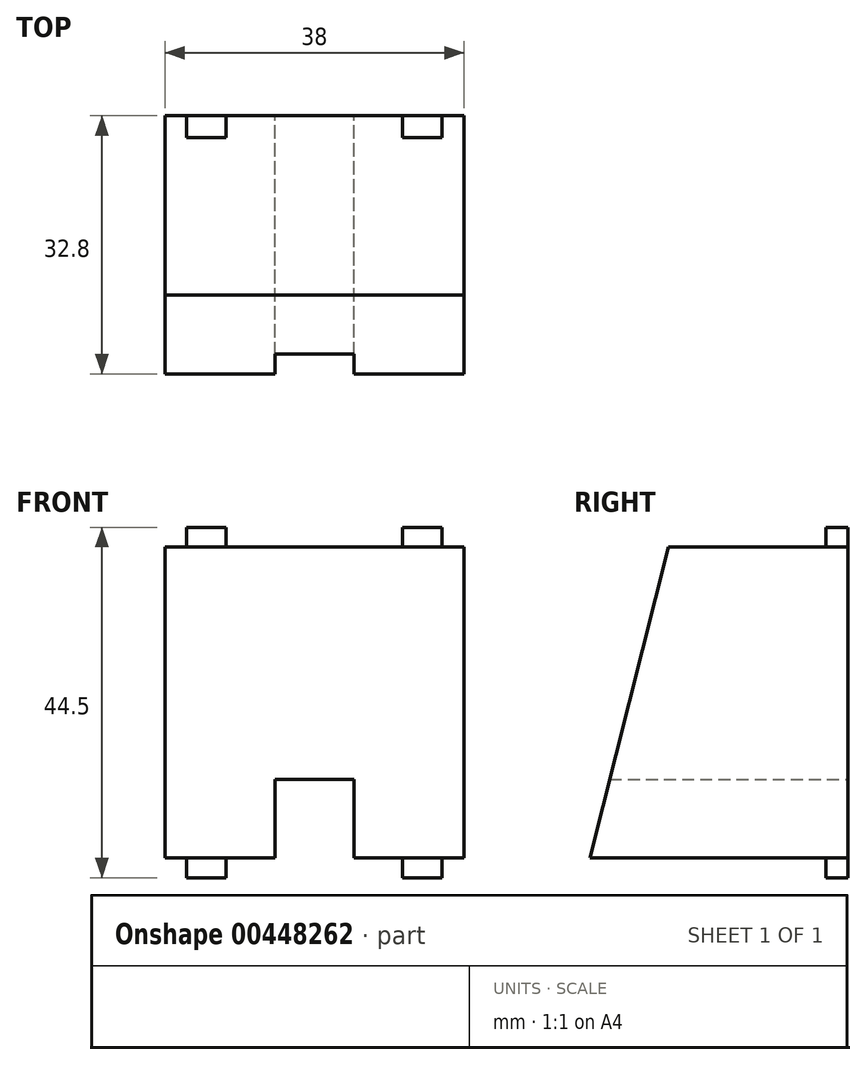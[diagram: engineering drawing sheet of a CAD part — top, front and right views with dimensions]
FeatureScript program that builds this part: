
annotation { "Feature Type Name" : "Feature", "Feature Type Description" : "" }
export const myFeature = defineFeature(function(context is Context, id is Id, definition is map)
    precondition{}
    {
        {
            var Q0;
            Q0=qCreatedBy(makeId("Front.planeOp"),FACE);
            var sketch = newSketch(context, id + "F0", { "sketchPlane" : qUnion([Q0])});
            skLineSegment(sketch, "E0", {"start": v(0, 0) * mm, "end": v(-11.22, 0) * mm});
            skLineSegment(sketch, "E1", {"start": v(-11.22, 0) * mm, "end": v(-11.22, 2.5) * mm});
            skLineSegment(sketch, "E2", {"start": v(-11.22, 2.5) * mm, "end": v(-16.22, 2.5) * mm});
            skLineSegment(sketch, "E3", {"start": v(-16.22, 2.5) * mm, "end": v(-16.22, 0) * mm});
            skLineSegment(sketch, "E4", {"start": v(-16.22, 0) * mm, "end": v(-19, 0) * mm});
            skLineSegment(sketch, "E5", {"start": v(-19, 0) * mm, "end": v(-19, -39.5) * mm});
            skLineSegment(sketch, "E6", {"start": v(-19, -39.5) * mm, "end": v(-16.22, -39.5) * mm});
            skLineSegment(sketch, "E7", {"start": v(-16.22, -39.5) * mm, "end": v(-16.22, -42) * mm});
            skLineSegment(sketch, "E8", {"start": v(-16.22, -42) * mm, "end": v(-11.22, -42) * mm});
            skLineSegment(sketch, "E9", {"start": v(-11.22, -42) * mm, "end": v(-11.22, -39.5) * mm});
            skLineSegment(sketch, "E10", {"start": v(-11.22, -39.5) * mm, "end": v(0, -39.5) * mm});
            skLineSegment(sketch, "E11.MirrorCS", {"start": v(11.22, 0) * mm, "end": v(11.22, 2.5) * mm});
            skLineSegment(sketch, "E12.MirrorCS", {"start": v(11.22, -42) * mm, "end": v(11.22, -39.5) * mm});
            skLineSegment(sketch, "E13.MirrorCS", {"start": v(16.22, 0) * mm, "end": v(19, 0) * mm});
            skLineSegment(sketch, "E14.MirrorCS", {"start": v(16.22, -42) * mm, "end": v(11.22, -42) * mm});
            skLineSegment(sketch, "E15.MirrorCS", {"start": v(19, 0) * mm, "end": v(19, -39.5) * mm});
            skLineSegment(sketch, "E16.MirrorCS", {"start": v(11.22, 2.5) * mm, "end": v(16.22, 2.5) * mm});
            skLineSegment(sketch, "E17.MirrorCS", {"start": v(19, -39.5) * mm, "end": v(16.22, -39.5) * mm});
            skLineSegment(sketch, "E18.MirrorCS", {"start": v(16.22, 2.5) * mm, "end": v(16.22, 0) * mm});
            skLineSegment(sketch, "E19.MirrorCS", {"start": v(16.22, -39.5) * mm, "end": v(16.22, -42) * mm});
            skLineSegment(sketch, "E20.MirrorCS", {"start": v(11.22, -39.5) * mm, "end": v(0, -39.5) * mm});
            skLineSegment(sketch, "E21.MirrorCS", {"start": v(0, 0) * mm, "end": v(11.22, 0) * mm});
            skLineSegment(sketch, "E22", {"start": v(-16.22, 0) * mm, "end": v(-11.22, 0) * mm});
            skLineSegment(sketch, "E23", {"start": v(11.22, 0) * mm, "end": v(16.22, 0) * mm});
            skLineSegment(sketch, "E24", {"start": v(-16.22, -39.5) * mm, "end": v(-11.22, -39.5) * mm});
            skLineSegment(sketch, "E25", {"start": v(11.22, -39.5) * mm, "end": v(16.22, -39.5) * mm});
            skSolve(sketch);
        }
        {
            var Q0;
            Q0=makeQuery(id+"F0.imprint","IMPRINT",FACE,{"disambiguationData":[TD([[makeQuery(id+"F0.imprint","IMPRINT",EDGE,{"derivedFrom":sQuery(id+"F0.wireOp",EDGE,"E1")}),1.0]])]});
            var Q1;
            Q1=makeQuery(id+"F0.imprint","IMPRINT",FACE,{"disambiguationData":[TD([[makeQuery(id+"F0.imprint","IMPRINT",EDGE,{"derivedFrom":sQuery(id+"F0.wireOp",EDGE,"E11.MirrorCS")}),-1.0]])]});
            var Q2;
            Q2=makeQuery(id+"F0.imprint","IMPRINT",FACE,{"disambiguationData":[TD([[makeQuery(id+"F0.imprint","IMPRINT",EDGE,{"derivedFrom":sQuery(id+"F0.wireOp",EDGE,"E7")}),1.0]])]});
            var Q3;
            Q3=makeQuery(id+"F0.imprint","IMPRINT",FACE,{"disambiguationData":[TD([[makeQuery(id+"F0.imprint","IMPRINT",EDGE,{"derivedFrom":sQuery(id+"F0.wireOp",EDGE,"E12.MirrorCS")}),-1.0]])]});
            var Q4;
            Q4=makeQuery(id+"F0.imprint","IMPRINT",FACE,{"disambiguationData":[TD([[makeQuery(id+"F0.imprint","IMPRINT",EDGE,{"derivedFrom":sQuery(id+"F0.wireOp",EDGE,"E0")}),1.0]])]});
            extrude(context, id + "F1", {"entities" : qUnion([Q0, Q1, Q2, Q3, Q4]), "depth" : 2.8 * mm});
        }
        {
            var Q0;
            Q0=makeQuery(id+"F1.opExtrude","SWEPT_FACE",FACE,{"disambiguationData":[OSD([sQuery(id+"F0.wireOp",EDGE,"E5")])]});
            var sketch = newSketch(context, id + "F2", { "sketchPlane" : qUnion([Q0])});
            skLineSegment(sketch, "E26", {"start": v(2.8, -39.5) * mm, "end": v(32.8, -39.5) * mm});
            skLineSegment(sketch, "E27", {"start": v(32.8, -39.5) * mm, "end": v(22.8, 0) * mm});
            skLineSegment(sketch, "E28", {"start": v(22.8, 0) * mm, "end": v(2.8, 0) * mm});
            skSolve(sketch);
        }
        {
            var Q0;
            Q0=makeQuery(id+"F2.imprint","IMPRINT",FACE,{"disambiguationData":[TD([[makeQuery(id+"F2.imprint","IMPRINT",EDGE,{"derivedFrom":sQuery(id+"F2.wireOp",EDGE,"E26")}),1.0]])]});
            extrude(context, id + "F3", {"entities" : qUnion([Q0]), "operationType" : NewBodyOperationType.ADD, "oppositeDirection" : true, "depth" : 38 * mm});
        }
        {
            var Q0;
            Q0=makeQuery(id+"F0.imprint","IMPRINT",FACE,{"disambiguationData":[TD([[makeQuery(id+"F0.imprint","IMPRINT",EDGE,{"derivedFrom":sQuery(id+"F0.wireOp",EDGE,"E0")}),1.0]])]});
            var sketch = newSketch(context, id + "F4", { "sketchPlane" : qUnion([Q0])});
            skLineSegment(sketch, "E29.bottom", {"start": v(-5, -39.5) * mm, "end": v(5, -39.5) * mm});
            skLineSegment(sketch, "E29.top", {"start": v(-5, -29.5) * mm, "end": v(5, -29.5) * mm});
            skLineSegment(sketch, "E29.left", {"start": v(-5, -39.5) * mm, "end": v(-5, -29.5) * mm});
            skLineSegment(sketch, "E29.right", {"start": v(5, -39.5) * mm, "end": v(5, -29.5) * mm});
            skPoint(sketch, "E29.middle", {"position": v(0, -34.5) * mm});
            skSolve(sketch);
        }
        {
            var Q0;
            Q0=makeQuery(id+"F4.imprint","IMPRINT",FACE,{"disambiguationData":[TD([[makeQuery(id+"F4.imprint","IMPRINT",EDGE,{"derivedFrom":sQuery(id+"F4.wireOp",EDGE,"E29.bottom")}),1.0]])]});
            extrude(context, id + "F5", {"entities" : qUnion([Q0]), "operationType" : NewBodyOperationType.REMOVE, "depth" : 40 * mm});
        }
    });
